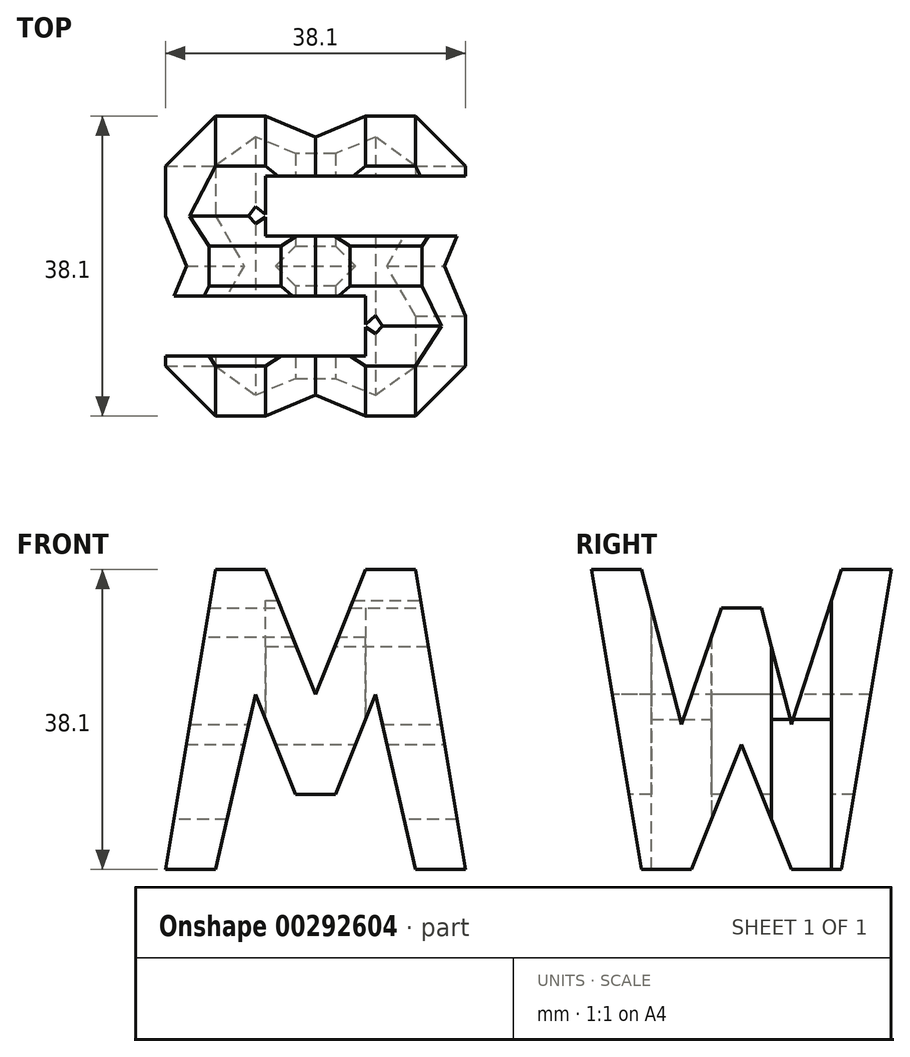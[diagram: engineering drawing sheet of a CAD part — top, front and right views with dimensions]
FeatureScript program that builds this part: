
annotation { "Feature Type Name" : "Feature", "Feature Type Description" : "" }
export const myFeature = defineFeature(function(context is Context, id is Id, definition is map)
    precondition{}
    {
        {
            var Q0;
            Q0=qCreatedBy(makeId("Front.planeOp"),FACE);
            var sketch = newSketch(context, id + "F0", { "sketchPlane" : qUnion([Q0])});
            skLineSegment(sketch, "E0", {"start": v(0, 0) * mm, "end": v(38.1, 0) * mm});
            skLineSegment(sketch, "E1", {"start": v(38.1, 0) * mm, "end": v(38.1, 38.1) * mm});
            skLineSegment(sketch, "E2", {"start": v(38.1, 38.1) * mm, "end": v(0, 38.1) * mm});
            skLineSegment(sketch, "E3", {"start": v(0, 38.1) * mm, "end": v(0, 0) * mm});
            skSolve(sketch);
        }
        {
            var Q0;
            Q0 = qSketchRegion(id + "F0", true);
            extrude(context, id + "F1", {"entities" : qUnion([Q0]), "depth" : 38.1 * mm});
        }
        {
            var Q0;
            Q0=qCreatedBy(makeId("Front.planeOp"),FACE);
            cPlane(context, id + "F2", {"entities" : qUnion([Q0]), "cplaneType" : CPlaneType.OFFSET, "offset" : 38.1 * mm, "width" : 152.4 * mm, "height" : 152.4 * mm});
        }
        {
            var Q0;
            Q0=qCreatedBy(makeId("Right.planeOp"),FACE);
            cPlane(context, id + "F3", {"entities" : qUnion([Q0]), "cplaneType" : CPlaneType.OFFSET, "offset" : 38.1 * mm, "width" : 152.4 * mm, "height" : 152.4 * mm});
        }
        {
            var Q0;
            Q0=qCreatedBy(makeId("Top.planeOp"),FACE);
            cPlane(context, id + "F4", {"entities" : qUnion([Q0]), "cplaneType" : CPlaneType.OFFSET, "offset" : 38.1 * mm, "width" : 152.4 * mm, "height" : 152.4 * mm});
        }
        {
            var Q0;
            Q0=qCreatedBy(id+"F3.planeOp",FACE);
            var sketch = newSketch(context, id + "F5", { "sketchPlane" : qUnion([Q0])});
            skLineSegment(sketch, "E4", {"start": v(0, 0) * mm, "end": v(-38.1, 0) * mm});
            skLineSegment(sketch, "E5", {"start": v(-38.1, 0) * mm, "end": v(-38.1, 38.1) * mm});
            skLineSegment(sketch, "E6", {"start": v(-38.1, 38.1) * mm, "end": v(0, 38.1) * mm});
            skLineSegment(sketch, "E7", {"start": v(0, 38.1) * mm, "end": v(0, 0) * mm});
            skLineSegment(sketch, "E8", {"start": v(-38.1, 38.1) * mm, "end": v(-31.75, 0) * mm});
            skLineSegment(sketch, "E9", {"start": v(-6.35, 0) * mm, "end": v(0, 38.1) * mm});
            skLineSegment(sketch, "E10", {"start": v(-31.75, 38.1) * mm, "end": v(-26.67, 18.44) * mm});
            skLineSegment(sketch, "E11", {"start": v(-26.67, 18.44) * mm, "end": v(-21.59, 33.18) * mm});
            skLineSegment(sketch, "E12", {"start": v(-16.5, 33.18) * mm, "end": v(-12.7, 18.44) * mm});
            skLineSegment(sketch, "E13", {"start": v(-21.59, 33.18) * mm, "end": v(-16.5, 33.18) * mm});
            skLineSegment(sketch, "E14", {"start": v(-12.7, 18.44) * mm, "end": v(-6.35, 38.1) * mm});
            skLineSegment(sketch, "E15", {"start": v(-25.4, 0) * mm, "end": v(-19.05, 15.88) * mm});
            skPoint(sketch, "E15.endSnap0", {"position": v(-19.05, 38.1) * mm});
            skLineSegment(sketch, "E16", {"start": v(-19.05, 15.88) * mm, "end": v(-12.7, 0) * mm});
            skSolve(sketch);
        }
        {
            var Q0;
            {var subQ0=sQuery(id+"F5.wireOp",EDGE,"E5");Q0=makeQuery(id+"F5.imprint","IMPRINT",FACE,{"disambiguationData":[TD([[makeQuery(id+"F5.imprint","IMPRINT",EDGE,{"derivedFrom":subQ0}),-1.0]])]});}
            var Q1;
            {var subQ0=sQuery(id+"F5.wireOp",EDGE,"E10");Q1=makeQuery(id+"F5.imprint","IMPRINT",FACE,{"disambiguationData":[TD([[makeQuery(id+"F5.imprint","IMPRINT",EDGE,{"derivedFrom":subQ0}),1.0]])]});}
            var Q2;
            {var subQ0=sQuery(id+"F5.wireOp",EDGE,"E15");Q2=makeQuery(id+"F5.imprint","IMPRINT",FACE,{"disambiguationData":[TD([[makeQuery(id+"F5.imprint","IMPRINT",EDGE,{"derivedFrom":subQ0}),-1.0]])]});}
            var Q3;
            {var subQ0=sQuery(id+"F5.wireOp",EDGE,"E7");Q3=makeQuery(id+"F5.imprint","IMPRINT",FACE,{"disambiguationData":[TD([[makeQuery(id+"F5.imprint","IMPRINT",EDGE,{"derivedFrom":subQ0}),-1.0]])]});}
            extrude(context, id + "F6", {"entities" : qUnion([Q0, Q1, Q2, Q3]), "operationType" : NewBodyOperationType.REMOVE, "oppositeDirection" : true, "depth" : 38.1 * mm});
        }
        {
            var Q0;
            Q0=qCreatedBy(id+"F2.planeOp",FACE);
            var sketch = newSketch(context, id + "F7", { "sketchPlane" : qUnion([Q0])});
            skLineSegment(sketch, "E17", {"start": v(0, 0) * mm, "end": v(38.1, 0) * mm});
            skLineSegment(sketch, "E18", {"start": v(38.1, 0) * mm, "end": v(38.1, 38.1) * mm});
            skLineSegment(sketch, "E19", {"start": v(38.1, 38.1) * mm, "end": v(0, 38.1) * mm});
            skLineSegment(sketch, "E20", {"start": v(0, 38.1) * mm, "end": v(0, 0) * mm});
            skLineSegment(sketch, "E21", {"start": v(6.35, 0) * mm, "end": v(11.43, 22.23) * mm});
            skLineSegment(sketch, "E22", {"start": v(11.43, 22.23) * mm, "end": v(16.51, 9.52) * mm});
            skLineSegment(sketch, "E23", {"start": v(16.51, 9.52) * mm, "end": v(21.6, 9.52) * mm});
            skLineSegment(sketch, "E24", {"start": v(21.6, 9.52) * mm, "end": v(26.67, 22.23) * mm});
            skLineSegment(sketch, "E25", {"start": v(26.67, 22.23) * mm, "end": v(31.75, 0) * mm});
            skLineSegment(sketch, "E26", {"start": v(0, 0) * mm, "end": v(6.35, 38.1) * mm});
            skLineSegment(sketch, "E27", {"start": v(12.7, 38.1) * mm, "end": v(19.05, 22.22) * mm});
            skPoint(sketch, "E27.endSnap0", {"position": v(19.05, 38.1) * mm});
            skLineSegment(sketch, "E28", {"start": v(19.05, 22.22) * mm, "end": v(25.4, 38.1) * mm});
            skLineSegment(sketch, "E29", {"start": v(31.75, 38.1) * mm, "end": v(38.1, 0) * mm});
            skSolve(sketch);
        }
        {
            var Q0;
            {var subQ0=sQuery(id+"F7.wireOp",EDGE,"E20");Q0=makeQuery(id+"F7.imprint","IMPRINT",FACE,{"disambiguationData":[TD([[makeQuery(id+"F7.imprint","IMPRINT",EDGE,{"derivedFrom":subQ0}),1.0]])]});}
            var Q1;
            {var subQ0=sQuery(id+"F7.wireOp",EDGE,"E21");Q1=makeQuery(id+"F7.imprint","IMPRINT",FACE,{"disambiguationData":[TD([[makeQuery(id+"F7.imprint","IMPRINT",EDGE,{"derivedFrom":subQ0}),-1.0]])]});}
            var Q2;
            {var subQ0=sQuery(id+"F7.wireOp",EDGE,"E27");Q2=makeQuery(id+"F7.imprint","IMPRINT",FACE,{"disambiguationData":[TD([[makeQuery(id+"F7.imprint","IMPRINT",EDGE,{"derivedFrom":subQ0}),1.0]])]});}
            var Q3;
            {var subQ0=sQuery(id+"F7.wireOp",EDGE,"E18");Q3=makeQuery(id+"F7.imprint","IMPRINT",FACE,{"disambiguationData":[TD([[makeQuery(id+"F7.imprint","IMPRINT",EDGE,{"derivedFrom":subQ0}),1.0]])]});}
            extrude(context, id + "F8", {"entities" : qUnion([Q0, Q1, Q2, Q3]), "operationType" : NewBodyOperationType.REMOVE, "oppositeDirection" : true, "depth" : 38.1 * mm});
        }
        {
            var Q0;
            Q0=qCreatedBy(id+"F4.planeOp",FACE);
            var sketch = newSketch(context, id + "F9", { "sketchPlane" : qUnion([Q0])});
            skLineSegment(sketch, "E30", {"start": v(0, 0) * mm, "end": v(38.1, 0) * mm});
            skLineSegment(sketch, "E31", {"start": v(38.1, 0) * mm, "end": v(38.1, -38.1) * mm});
            skLineSegment(sketch, "E32", {"start": v(38.1, -38.1) * mm, "end": v(0, -38.1) * mm});
            skLineSegment(sketch, "E33", {"start": v(0, -38.1) * mm, "end": v(0, 0) * mm});
            skLineSegment(sketch, "E34", {"start": v(12.7, -7.62) * mm, "end": v(12.7, -15.24) * mm});
            skLineSegment(sketch, "E35", {"start": v(12.7, -15.24) * mm, "end": v(38.1, -15.24) * mm});
            skLineSegment(sketch, "E36", {"start": v(38.1, -15.24) * mm, "end": v(38.1, -7.62) * mm});
            skLineSegment(sketch, "E37", {"start": v(38.1, -7.62) * mm, "end": v(12.7, -7.62) * mm});
            skLineSegment(sketch, "E38", {"start": v(0, -22.86) * mm, "end": v(25.4, -22.86) * mm});
            skLineSegment(sketch, "E39", {"start": v(25.4, -22.86) * mm, "end": v(25.4, -30.48) * mm});
            skLineSegment(sketch, "E40", {"start": v(25.4, -30.48) * mm, "end": v(0, -30.48) * mm});
            skLineSegment(sketch, "E41", {"start": v(0, -30.48) * mm, "end": v(0, -22.86) * mm});
            skSolve(sketch);
        }
        {
            var Q0;
            Q0=makeQuery(id+"F9.imprint","IMPRINT",FACE,{"disambiguationData":[TD([[makeQuery(id+"F9.imprint","IMPRINT",EDGE,{"derivedFrom":sQuery(id+"F9.wireOp",EDGE,"E34")}),1.0]])]});
            var Q1;
            Q1=makeQuery(id+"F9.imprint","IMPRINT",FACE,{"disambiguationData":[TD([[makeQuery(id+"F9.imprint","IMPRINT",EDGE,{"derivedFrom":sQuery(id+"F9.wireOp",EDGE,"E38")}),-1.0]])]});
            extrude(context, id + "F10", {"entities" : qUnion([Q0, Q1]), "operationType" : NewBodyOperationType.REMOVE, "oppositeDirection" : true, "depth" : 38.1 * mm});
        }
    });
